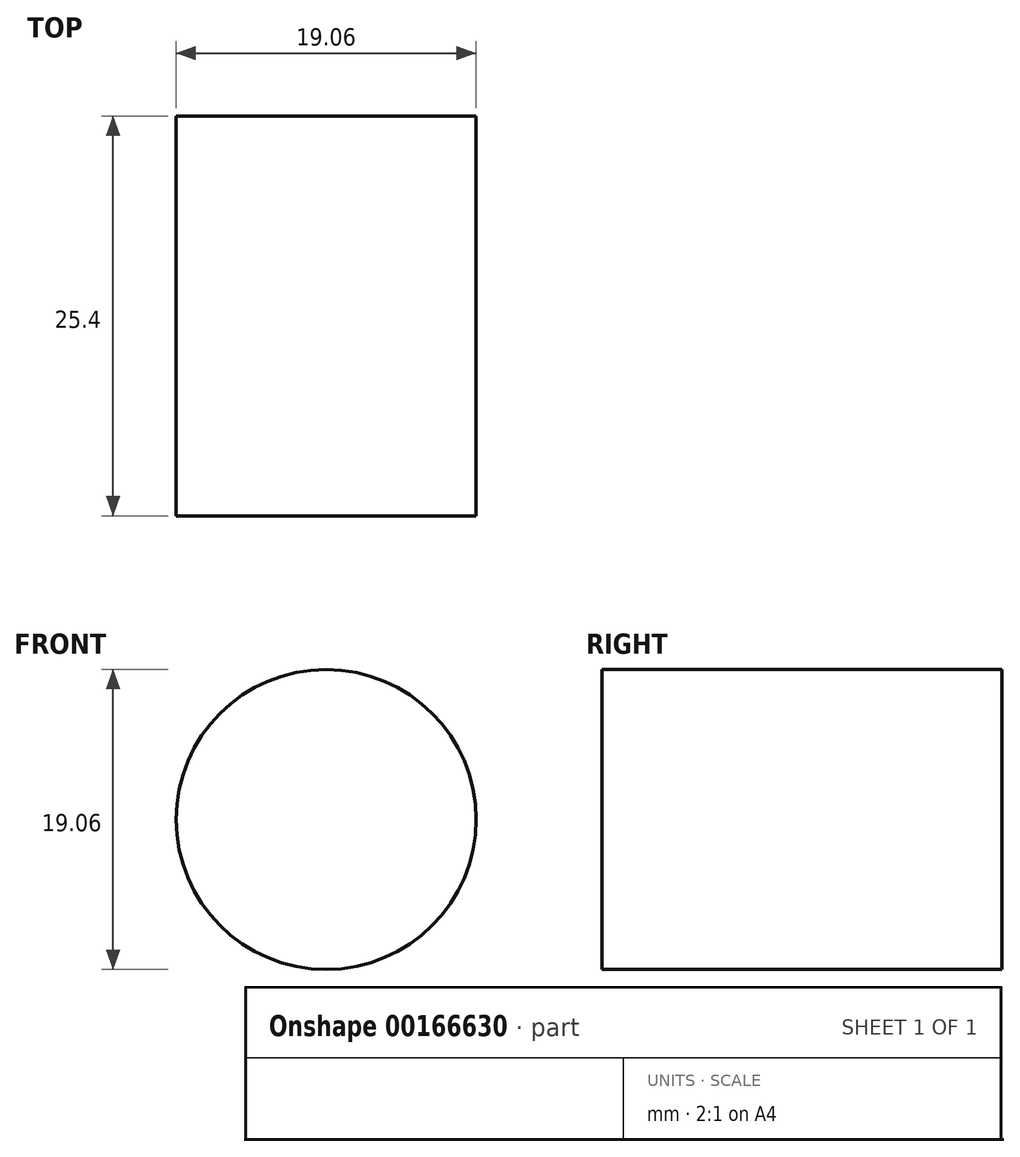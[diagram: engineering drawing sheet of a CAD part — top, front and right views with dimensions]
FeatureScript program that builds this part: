
annotation { "Feature Type Name" : "Feature", "Feature Type Description" : "" }
export const myFeature = defineFeature(function(context is Context, id is Id, definition is map)
    precondition{}
    {
        {
            var Q0;
            Q0=qCreatedBy(makeId("Front.planeOp"),FACE);
            var sketch = newSketch(context, id + "F0", { "sketchPlane" : qUnion([Q0])});
            skCircle(sketch, "E0", {"center": v(0, 0) * mm, "radius": 9.53 * mm});
            skSolve(sketch);
        }
        {
            var Q0;
            Q0 = qSketchRegion(id + "F0", true);
            extrude(context, id + "F1", {"entities" : qUnion([Q0]), "depth" : 25.4 * mm});
        }
        {
            var Q0;
            Q0=qCreatedBy(makeId("Front.planeOp"),FACE);
            var sketch = newSketch(context, id + "F2", { "sketchPlane" : qUnion([Q0])});
            skLineSegment(sketch, "E1.bottom", {"start": v(4.76, -4.76) * mm, "end": v(-4.76, -4.76) * mm});
            skLineSegment(sketch, "E1.top", {"start": v(4.76, 4.76) * mm, "end": v(-4.76, 4.76) * mm});
            skLineSegment(sketch, "E1.left", {"start": v(4.76, -4.76) * mm, "end": v(4.76, 4.76) * mm});
            skLineSegment(sketch, "E1.right", {"start": v(-4.76, -4.76) * mm, "end": v(-4.76, 4.76) * mm});
            skPoint(sketch, "E1.middle", {"position": v(0, 0) * mm});
            skCircle(sketch, "E2", {"center": v(0, 0) * mm, "radius": 4.76 * mm});
            skSolve(sketch);
        }
        {
            var Q0;
            {var subQ0=sQuery(id+"F2.wireOp",EDGE,"E1.left");var subQ1=sQuery(id+"F2.wireOp",EDGE,"E1.bottom");var subQ2=makeQuery(id+"F2.imprint","INTERSECT",VERTEX,{"derivedFrom":[subQ1,subQ0]});Q0=makeQuery(id+"F2.imprint","IMPRINT",FACE,{"disambiguationData":[TD([[makeQuery(id+"F2.imprint","IMPRINT",EDGE,{"disambiguationData":[TD([[subQ2,-1.0]])],"derivedFrom":subQ1}),-1.0]])]});}
            var Q1;
            {var subQ0=sQuery(id+"F2.wireOp",EDGE,"E1.right");var subQ1=sQuery(id+"F2.wireOp",EDGE,"E1.bottom");var subQ2=makeQuery(id+"F2.imprint","INTERSECT",VERTEX,{"derivedFrom":[subQ1,subQ0]});Q1=makeQuery(id+"F2.imprint","IMPRINT",FACE,{"disambiguationData":[TD([[makeQuery(id+"F2.imprint","IMPRINT",EDGE,{"disambiguationData":[TD([[subQ2,1.0]])],"derivedFrom":subQ1}),-1.0]])]});}
            var Q2;
            {var subQ0=sQuery(id+"F2.wireOp",EDGE,"E1.left");var subQ1=sQuery(id+"F2.wireOp",EDGE,"E1.top");var subQ2=makeQuery(id+"F2.imprint","INTERSECT",VERTEX,{"derivedFrom":[subQ1,subQ0]});Q2=makeQuery(id+"F2.imprint","IMPRINT",FACE,{"disambiguationData":[TD([[makeQuery(id+"F2.imprint","IMPRINT",EDGE,{"disambiguationData":[TD([[subQ2,-1.0]])],"derivedFrom":subQ1}),1.0]])]});}
            var Q3;
            {var subQ0=sQuery(id+"F2.wireOp",EDGE,"E1.right");var subQ1=sQuery(id+"F2.wireOp",EDGE,"E1.top");var subQ2=makeQuery(id+"F2.imprint","INTERSECT",VERTEX,{"derivedFrom":[subQ1,subQ0]});Q3=makeQuery(id+"F2.imprint","IMPRINT",FACE,{"disambiguationData":[TD([[makeQuery(id+"F2.imprint","IMPRINT",EDGE,{"disambiguationData":[TD([[subQ2,1.0]])],"derivedFrom":subQ1}),1.0]])]});}
            var Q4;
            Q4=makeQuery(id+"F1.opExtrude","CAP_FACE",FACE,{"disambiguationData":[OSD([sQuery(id+"F0.wireOp",EDGE,"E0")])],"isStart":true});
            extrude(context, id + "F3", {"entities" : qUnion([Q0, Q1, Q2, Q3, Q4]), "operationType" : NewBodyOperationType.REMOVE, "endBound" : BoundingType.THROUGH_ALL, "oppositeDirection" : true, "depth" : 25.4 * mm});
        }
    });
